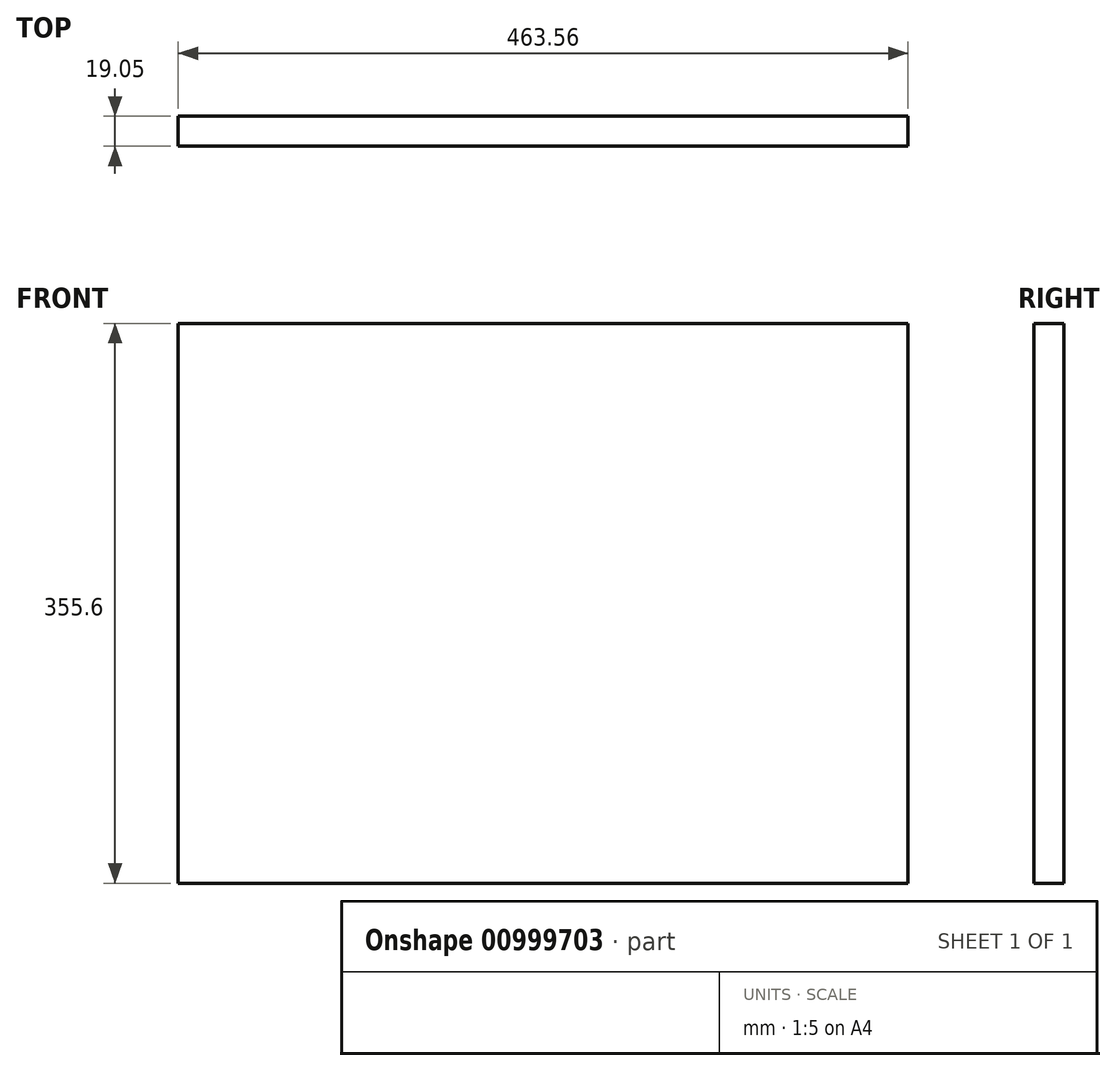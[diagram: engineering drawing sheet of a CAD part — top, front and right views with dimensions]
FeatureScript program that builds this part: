
annotation { "Feature Type Name" : "Feature", "Feature Type Description" : "" }
export const myFeature = defineFeature(function(context is Context, id is Id, definition is map)
    precondition{}
    {
        {
            var Q0;
            Q0=qCreatedBy(makeId("Front.planeOp"),FACE);
            var sketch = newSketch(context, id + "F0", { "sketchPlane" : qUnion([Q0])});
            skLineSegment(sketch, "E0.bottom", {"start": v(-231.78, -177.8) * mm, "end": v(231.78, -177.8) * mm});
            skLineSegment(sketch, "E0.top", {"start": v(-231.78, 177.8) * mm, "end": v(231.77, 177.8) * mm});
            skLineSegment(sketch, "E0.left", {"start": v(-231.77, -177.8) * mm, "end": v(-231.78, 177.8) * mm});
            skLineSegment(sketch, "E0.right", {"start": v(231.78, -177.8) * mm, "end": v(231.77, 177.8) * mm});
            skPoint(sketch, "E0.middle", {"position": v(0, 0) * mm});
            skSolve(sketch);
        }
        {
            var Q0;
            Q0 = qSketchRegion(id + "F0", true);
            extrude(context, id + "F1", {"entities" : qUnion([Q0]), "depth" : 19.05 * mm, "offsetDistance" : 25.4 * mm});
        }
    });
